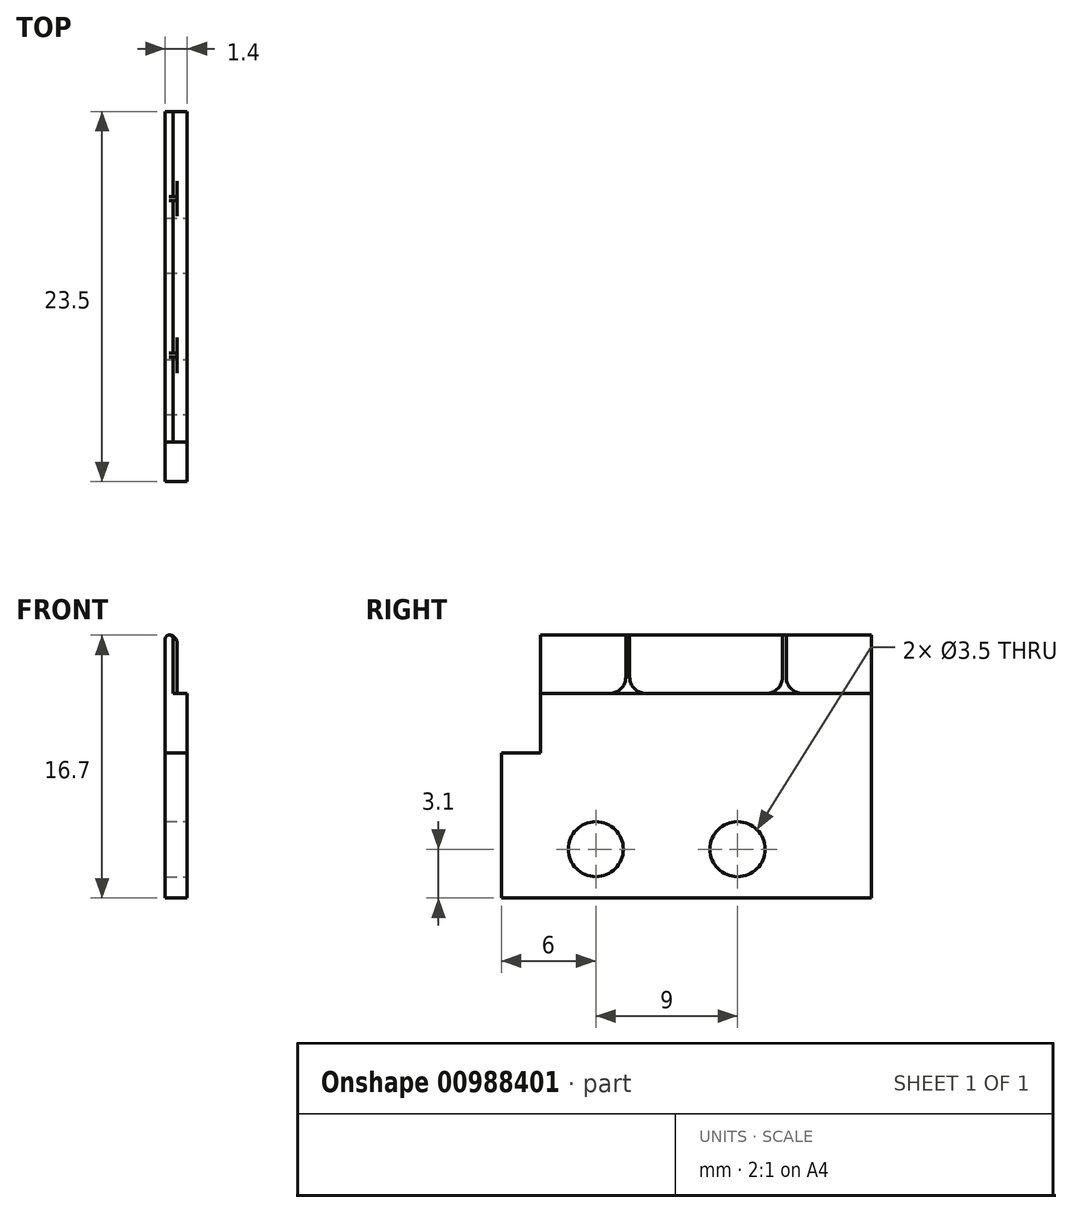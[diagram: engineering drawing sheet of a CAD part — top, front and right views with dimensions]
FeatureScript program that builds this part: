
annotation { "Feature Type Name" : "Feature", "Feature Type Description" : "" }
export const myFeature = defineFeature(function(context is Context, id is Id, definition is map)
    precondition{}
    {
        {
            var Q0;
            Q0=qCreatedBy(makeId("Right.planeOp"),FACE);
            var sketch = newSketch(context, id + "F0", { "sketchPlane" : qUnion([Q0])});
            skLineSegment(sketch, "E0", {"start": v(0, 0) * mm, "end": v(23.5, 0) * mm});
            skLineSegment(sketch, "E1", {"start": v(23.5, 0) * mm, "end": v(23.5, 13) * mm});
            skLineSegment(sketch, "E2", {"start": v(23.5, 13) * mm, "end": v(2.5, 13) * mm});
            skLineSegment(sketch, "E3", {"start": v(0, 0) * mm, "end": v(0, 9.2) * mm});
            skLineSegment(sketch, "E4", {"start": v(2.5, 13) * mm, "end": v(2.5, 9.2) * mm});
            skLineSegment(sketch, "E5", {"start": v(0, 9.2) * mm, "end": v(2.5, 9.2) * mm});
            skSolve(sketch);
        }
        {
            var Q0;
            Q0=makeQuery(id+"F0.imprint","IMPRINT",FACE,{"disambiguationData":[TD([[makeQuery(id+"F0.imprint","IMPRINT",EDGE,{"derivedFrom":sQuery(id+"F0.wireOp",EDGE,"E0")}),1.0]])]});
            extrude(context, id + "F1", {"entities" : qUnion([Q0]), "depth" : 1.4 * mm, "offsetDistance" : 25 * mm});
        }
        {
            var Q0;
            Q0=makeQuery(id+"F1.opExtrude","SWEPT_FACE",FACE,{"disambiguationData":[OSD([sQuery(id+"F0.wireOp",EDGE,"E2")])]});
            var sketch = newSketch(context, id + "F2", { "sketchPlane" : qUnion([Q0])});
            skLineSegment(sketch, "E6", {"start": v(0, 23.5) * mm, "end": v(0.5, 23.5) * mm});
            skLineSegment(sketch, "E7", {"start": v(0.5, 23.5) * mm, "end": v(0.5, 2.5) * mm});
            skLineSegment(sketch, "E8", {"start": v(0.5, 2.5) * mm, "end": v(0, 2.5) * mm});
            skLineSegment(sketch, "E9", {"start": v(0, 2.5) * mm, "end": v(0, 23.5) * mm});
            skSolve(sketch);
        }
        {
            var Q0;
            Q0=makeQuery(id+"F2.imprint","IMPRINT",FACE,{"disambiguationData":[TD([[makeQuery(id+"F2.imprint","IMPRINT",EDGE,{"derivedFrom":sQuery(id+"F2.wireOp",EDGE,"E6")}),1.0]])]});
            extrude(context, id + "F3", {"entities" : qUnion([Q0]), "operationType" : NewBodyOperationType.ADD, "depth" : 3.7 * mm, "offsetDistance" : 25 * mm});
        }
        {
            var Q0;
            Q0=makeQuery(id+"F1.opExtrude","CAP_FACE",FACE,{"disambiguationData":[OSD([sQuery(id+"F0.wireOp",EDGE,"E0"),sQuery(id+"F0.wireOp",EDGE,"E1"),sQuery(id+"F0.wireOp",EDGE,"E2"),sQuery(id+"F0.wireOp",EDGE,"E3"),sQuery(id+"F0.wireOp",EDGE,"E4"),sQuery(id+"F0.wireOp",EDGE,"E5")])],"isStart":false});
            var sketch = newSketch(context, id + "F4", { "sketchPlane" : qUnion([Q0])});
            skCircle(sketch, "E10", {"center": v(6, 3.1) * mm, "radius": 1.75 * mm});
            skCircle(sketch, "E11", {"center": v(15, 3.1) * mm, "radius": 1.75 * mm});
            skSolve(sketch);
        }
        {
            var Q0;
            Q0=sQuery(id+"F4.wireOp",VERTEX,"E10.center");
            var Q1;
            Q1=sQuery(id+"F4.wireOp",VERTEX,"E11.center");
            var Q2;
            Q2=makeQuery(id+"F1.opExtrude","SWEPT_BODY",BODY,{"disambiguationData":[OSD([sQuery(id+"F0.wireOp",EDGE,"E0"),sQuery(id+"F0.wireOp",EDGE,"E1"),sQuery(id+"F0.wireOp",EDGE,"E2"),sQuery(id+"F0.wireOp",EDGE,"E3"),sQuery(id+"F0.wireOp",EDGE,"E4"),sQuery(id+"F0.wireOp",EDGE,"E5")])]});
            hole(context, id + "F5", {"style" : HoleStyle.SIMPLE, "endStyle" : HoleEndStyle.THROUGH, "holeDiameter" : 3.5 * mm, "majorDiameter" : 5 * mm, "isTappedThrough" : true, "tappedDepth" : 12 * mm, "tapClearance" : 3, "locations" : qUnion([Q0, Q1]), "scope" : qUnion([Q2])});
        }
        {
            var Q0;
            Q0=makeQuery(id+"F3.opExtrude","SWEPT_FACE",FACE,{"disambiguationData":[OSD([sQuery(id+"F2.wireOp",EDGE,"E7")])]});
            var sketch = newSketch(context, id + "F6", { "sketchPlane" : qUnion([Q0])});
            skLineSegment(sketch, "E12", {"start": v(7.9, 14) * mm, "end": v(7.9, 16.7) * mm});
            skLineSegment(sketch, "E13", {"start": v(7.9, 16.7) * mm, "end": v(8.15, 16.7) * mm});
            skLineSegment(sketch, "E14", {"start": v(8.15, 16.7) * mm, "end": v(8.15, 14) * mm});
            skLineSegment(sketch, "E15", {"start": v(8.15, 13) * mm, "end": v(7.9, 13) * mm});
            skLineSegment(sketch, "E16", {"start": v(17.85, 14) * mm, "end": v(17.85, 16.7) * mm});
            skLineSegment(sketch, "E17", {"start": v(17.85, 16.7) * mm, "end": v(18.1, 16.7) * mm});
            skLineSegment(sketch, "E18", {"start": v(18.1, 16.7) * mm, "end": v(18.1, 14) * mm});
            skLineSegment(sketch, "E19", {"start": v(18.1, 13) * mm, "end": v(17.85, 13) * mm});
            skLineSegment(sketch, "E20", {"start": v(2.5, 13) * mm, "end": v(6.9, 13) * mm});
            skPoint(sketch, "E21.visualSharp", {"position": v(7.9, 13) * mm});
            skArc(sketch, "E21.filletArc", {"start": v(6.9, 13) * mm, "mid": v(7.6, 13.3) * mm, "end": v(7.9, 14) * mm});
            skLineSegment(sketch, "E22", {"start": v(9.15, 13) * mm, "end": v(16.85, 13) * mm});
            skPoint(sketch, "E23.visualSharp", {"position": v(8.15, 13) * mm});
            skArc(sketch, "E23.filletArc", {"start": v(8.15, 14) * mm, "mid": v(8.44, 13.3) * mm, "end": v(9.15, 13) * mm});
            skPoint(sketch, "E24.visualSharp", {"position": v(17.85, 13) * mm});
            skArc(sketch, "E24.filletArc", {"start": v(16.85, 13) * mm, "mid": v(17.56, 13.3) * mm, "end": v(17.85, 14) * mm});
            skLineSegment(sketch, "E25", {"start": v(19.1, 13) * mm, "end": v(23.5, 13) * mm});
            skPoint(sketch, "E26.visualSharp", {"position": v(18.1, 13) * mm});
            skArc(sketch, "E26.filletArc", {"start": v(18.1, 14) * mm, "mid": v(18.4, 13.3) * mm, "end": v(19.1, 13) * mm});
            skLineSegment(sketch, "E27", {"start": v(16.85, 13) * mm, "end": v(19.1, 13) * mm});
            skLineSegment(sketch, "E28", {"start": v(9.15, 13) * mm, "end": v(6.9, 13) * mm});
            skSolve(sketch);
        }
        {
            var Q0;
            Q0=makeQuery(id+"F6.imprint","IMPRINT",FACE,{"disambiguationData":[TD([[makeQuery(id+"F6.imprint","IMPRINT",EDGE,{"derivedFrom":sQuery(id+"F6.wireOp",EDGE,"E12")}),-1.0]])]});
            var Q1;
            Q1=makeQuery(id+"F6.imprint","IMPRINT",FACE,{"disambiguationData":[TD([[makeQuery(id+"F6.imprint","IMPRINT",EDGE,{"derivedFrom":sQuery(id+"F6.wireOp",EDGE,"E16")}),-1.0]])]});
            extrude(context, id + "F7", {"entities" : qUnion([Q0, Q1]), "operationType" : NewBodyOperationType.ADD, "depth" : 0.25 * mm, "offsetDistance" : 25 * mm});
        }
        {
            var Q0;
            Q0=makeQuery(id+"F3.opExtrude","CAP_EDGE",EDGE,{"disambiguationData":[OSD([sQuery(id+"F2.wireOp",EDGE,"E9")])],"isStart":false});
            var Q1;
            {var subQ0=sQuery(id+"F2.wireOp",EDGE,"E7");Q1=makeQuery(id+"F7.boolean.opBoolean","SPLIT",EDGE,{"disambiguationData":[TD([makeQuery(id+"F1.opExtrude","SWEPT_FACE",FACE,{"disambiguationData":[OSD([sQuery(id+"F0.wireOp",EDGE,"E1")])]})])],"derivedFrom":makeQuery(id+"F3.opExtrude","CAP_EDGE",EDGE,{"disambiguationData":[OSD([subQ0])],"isStart":false})});}
            var Q2;
            {var subQ0=sQuery(id+"F2.wireOp",EDGE,"E7");Q2=makeQuery(id+"F7.boolean.opBoolean","SPLIT",EDGE,{"disambiguationData":[TD([makeQuery(id+"F7.opExtrude","SWEPT_FACE",FACE,{"disambiguationData":[OSD([sQuery(id+"F6.wireOp",EDGE,"E14")])]})])],"derivedFrom":makeQuery(id+"F3.opExtrude","CAP_EDGE",EDGE,{"disambiguationData":[OSD([subQ0])],"isStart":false})});}
            var Q3;
            {var subQ1=sQuery(id+"F2.wireOp",EDGE,"E7");Q3=makeQuery(id+"F7.boolean.opBoolean","SPLIT",EDGE,{"disambiguationData":[TD([makeQuery(id+"F1.opExtrude","SWEPT_FACE",FACE,{"disambiguationData":[OSD([sQuery(id+"F0.wireOp",EDGE,"E4")])]})])],"derivedFrom":makeQuery(id+"F3.opExtrude","CAP_EDGE",EDGE,{"disambiguationData":[OSD([subQ1])],"isStart":false})});}
            fillet(context, id + "F8", {"entities" : qUnion([Q0, Q1, Q2, Q3]), "radius" : 0.25 * mm, "tangentPropagation" : true, "allowEdgeOverflow" : false});
        }
        {
            var Q0;
            Q0=makeQuery(id+"F7.opExtrude","CAP_EDGE",EDGE,{"disambiguationData":[OSD([sQuery(id+"F6.wireOp",EDGE,"E13")])],"isStart":false});
            var Q1;
            Q1=makeQuery(id+"F7.opExtrude","CAP_EDGE",EDGE,{"disambiguationData":[OSD([sQuery(id+"F6.wireOp",EDGE,"E17")])],"isStart":false});
            fillet(context, id + "F9", {"entities" : qUnion([Q0, Q1]), "radius" : 0.5 * mm, "tangentPropagation" : true, "allowEdgeOverflow" : false});
        }
    });
